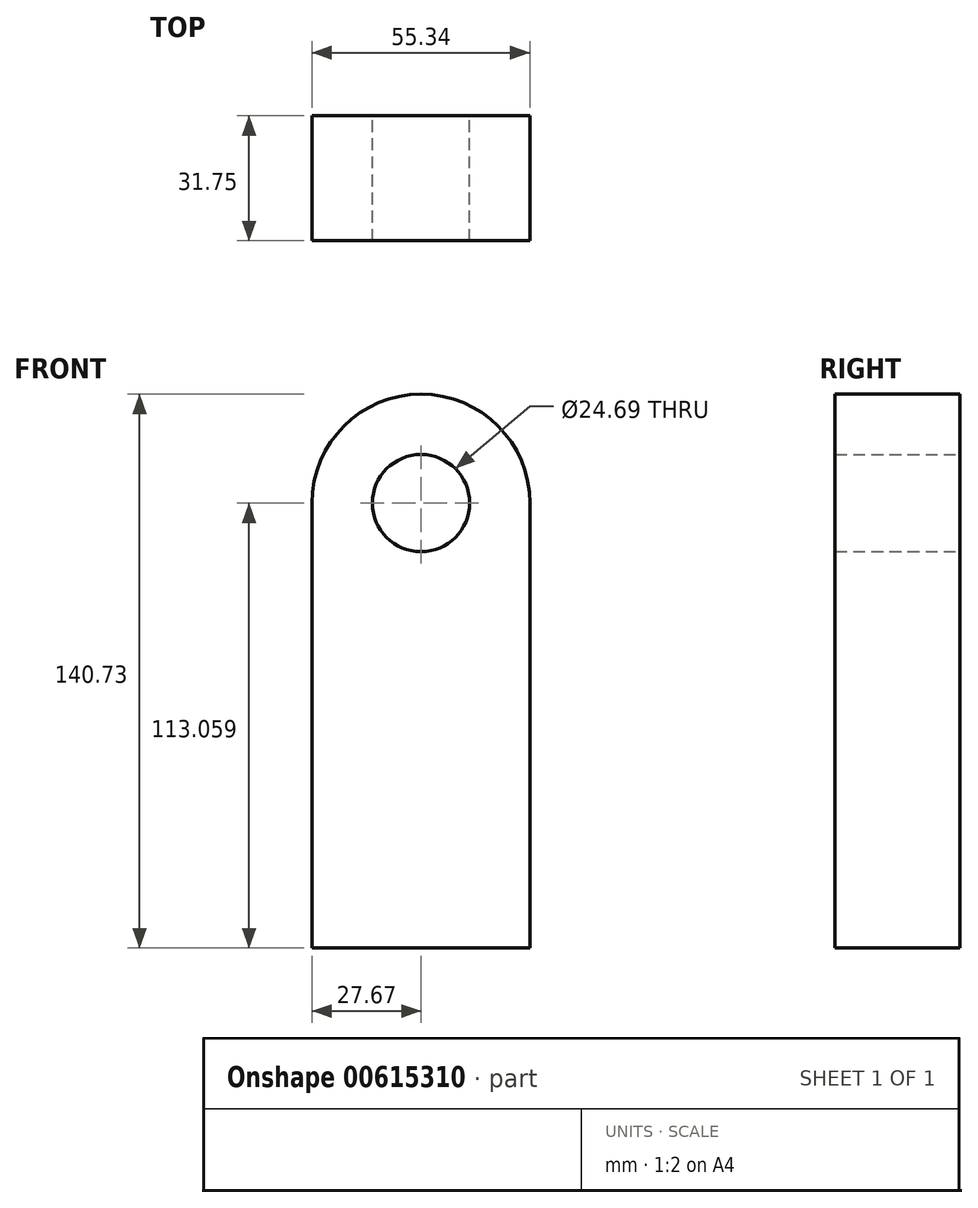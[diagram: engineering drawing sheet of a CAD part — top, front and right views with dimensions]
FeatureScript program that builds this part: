
annotation { "Feature Type Name" : "Feature", "Feature Type Description" : "" }
export const myFeature = defineFeature(function(context is Context, id is Id, definition is map)
    precondition{}
    {
        {
            var Q0;
            Q0=qCreatedBy(makeId("Front.planeOp"),FACE);
            var sketch = newSketch(context, id + "F0", { "sketchPlane" : qUnion([Q0])});
            skLineSegment(sketch, "E0.top", {"start": v(-27.67, -56.53) * mm, "end": v(27.67, -56.53) * mm});
            skLineSegment(sketch, "E0.left", {"start": v(-27.67, 56.53) * mm, "end": v(-27.67, -56.53) * mm});
            skLineSegment(sketch, "E0.right", {"start": v(27.67, 56.53) * mm, "end": v(27.67, -56.53) * mm});
            skPoint(sketch, "E0.middle", {"position": v(0, 0) * mm});
            skArc(sketch, "E1", {"start": v(27.67, 56.53) * mm, "mid": v(0, 84.2) * mm, "end": v(-27.67, 56.53) * mm});
            skCircle(sketch, "E2", {"center": v(0, 56.53) * mm, "radius": 12.35 * mm});
            skSolve(sketch);
        }
        {
            var Q0;
            Q0=makeQuery(id+"F0.imprint","IMPRINT",FACE,{"disambiguationData":[TD([[makeQuery(id+"F0.imprint","IMPRINT",EDGE,{"derivedFrom":sQuery(id+"F0.wireOp",EDGE,"E0.top")}),1.0]])]});
            extrude(context, id + "F1", {"entities" : qUnion([Q0]), "depth" : 31.75 * mm, "offsetDistance" : 25.4 * mm});
        }
    });
